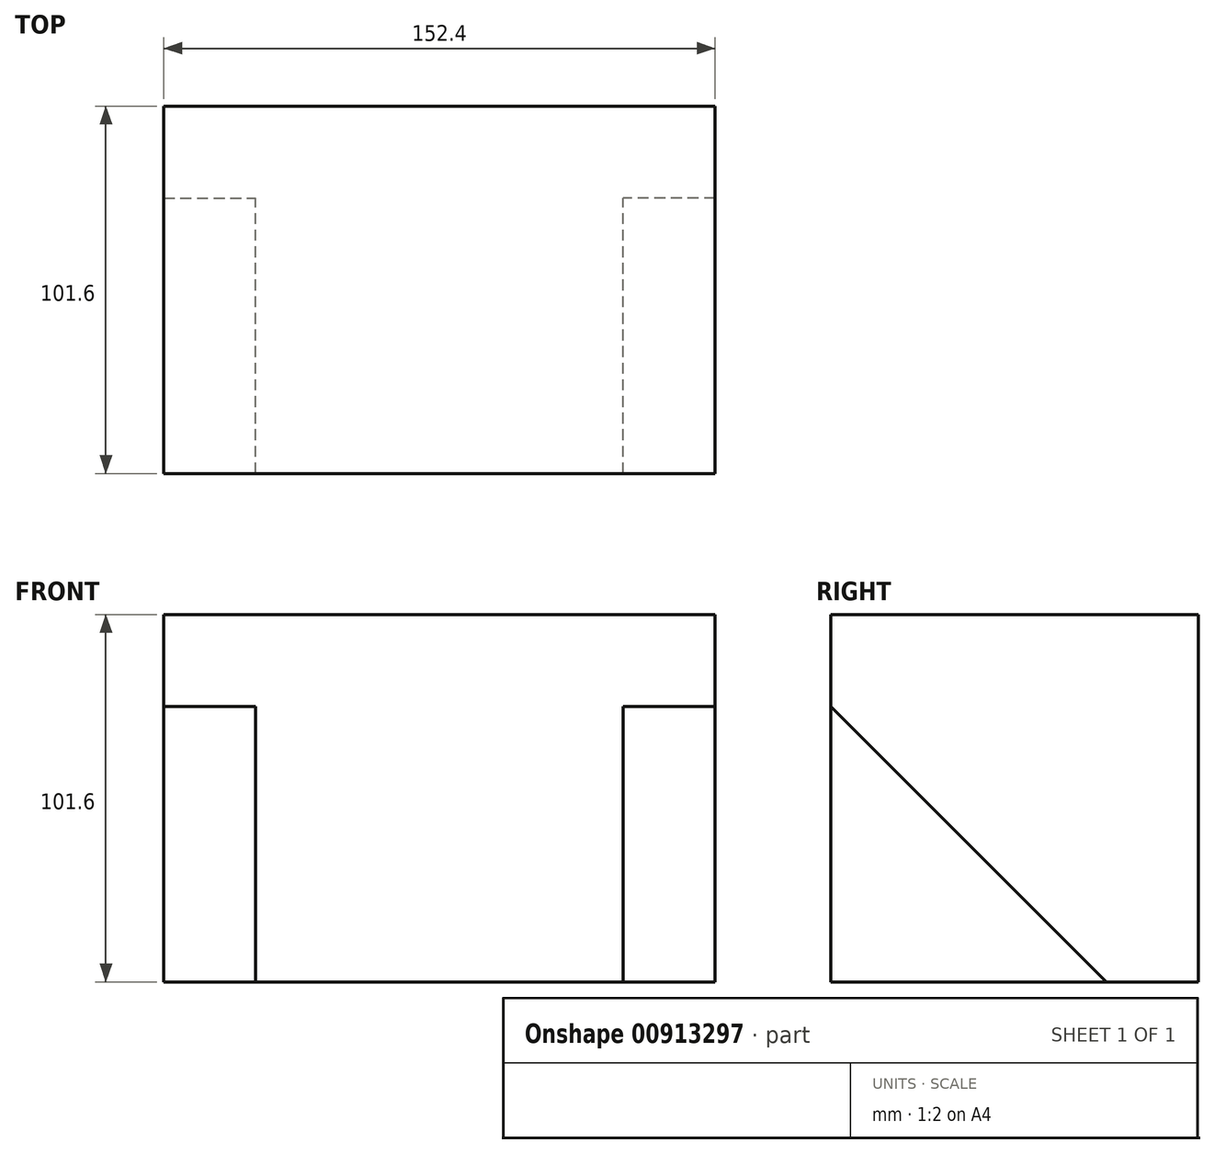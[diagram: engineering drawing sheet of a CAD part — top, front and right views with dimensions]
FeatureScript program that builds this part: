
annotation { "Feature Type Name" : "Feature", "Feature Type Description" : "" }
export const myFeature = defineFeature(function(context is Context, id is Id, definition is map)
    precondition{}
    {
        {
            var Q0;
            Q0=qCreatedBy(makeId("Top.planeOp"),FACE);
            var sketch = newSketch(context, id + "F0", { "sketchPlane" : qUnion([Q0])});
            skLineSegment(sketch, "E0.bottom", {"start": v(0, 0) * mm, "end": v(-101.6, 0) * mm});
            skLineSegment(sketch, "E0.top", {"start": v(0, 101.6) * mm, "end": v(-101.6, 101.6) * mm});
            skLineSegment(sketch, "E0.left", {"start": v(0, 0) * mm, "end": v(0, 101.6) * mm});
            skLineSegment(sketch, "E0.right", {"start": v(-101.6, 0) * mm, "end": v(-101.6, 101.6) * mm});
            skSolve(sketch);
        }
        {
            var Q0;
            Q0 = qSketchRegion(id + "F0", true);
            extrude(context, id + "F1", {"entities" : qUnion([Q0]), "depth" : 101.6 * mm, "offsetDistance" : 25.4 * mm});
        }
        {
            var Q0;
            Q0=makeQuery(id+"F1.opExtrude","CAP_FACE",FACE,{"disambiguationData":[OSD([sQuery(id+"F0.wireOp",EDGE,"E0.bottom"),sQuery(id+"F0.wireOp",EDGE,"E0.top"),sQuery(id+"F0.wireOp",EDGE,"E0.left"),sQuery(id+"F0.wireOp",EDGE,"E0.right")])],"isStart":false});
            var sketch = newSketch(context, id + "F2", { "sketchPlane" : qUnion([Q0])});
            skLineSegment(sketch, "E1.bottom", {"start": v(0, 0) * mm, "end": v(25.4, 0) * mm});
            skLineSegment(sketch, "E1.top", {"start": v(0, 101.6) * mm, "end": v(25.4, 101.6) * mm});
            skLineSegment(sketch, "E1.left", {"start": v(0, 0) * mm, "end": v(0, 101.6) * mm});
            skLineSegment(sketch, "E1.right", {"start": v(25.4, 0) * mm, "end": v(25.4, 101.6) * mm});
            skSolve(sketch);
        }
        {
            var Q0;
            Q0 = qSketchRegion(id + "F2", true);
            extrude(context, id + "F3", {"entities" : qUnion([Q0]), "oppositeDirection" : true, "depth" : 25.4 * mm, "offsetDistance" : 25.4 * mm});
        }
        {
            var Q0;
            Q0=makeQuery(id+"F1.opExtrude","SWEPT_FACE",FACE,{"disambiguationData":[OSD([sQuery(id+"F0.wireOp",EDGE,"E0.left")])]});
            var sketch = newSketch(context, id + "F4", { "sketchPlane" : qUnion([Q0])});
            skLineSegment(sketch, "E2.bottom", {"start": v(101.6, 0) * mm, "end": v(76.2, 0) * mm});
            skLineSegment(sketch, "E2.top", {"start": v(101.6, 76.2) * mm, "end": v(76.2, 76.2) * mm});
            skLineSegment(sketch, "E2.left", {"start": v(101.6, 0) * mm, "end": v(101.6, 76.2) * mm});
            skLineSegment(sketch, "E2.right", {"start": v(76.2, 0) * mm, "end": v(76.2, 76.2) * mm});
            skSolve(sketch);
        }
        {
            var Q0;
            Q0 = qSketchRegion(id + "F4", true);
            extrude(context, id + "F5", {"entities" : qUnion([Q0]), "depth" : 25.4 * mm, "offsetDistance" : 25.4 * mm});
        }
        {
            var Q0;
            Q0=makeQuery(id+"F1.opExtrude","SWEPT_FACE",FACE,{"disambiguationData":[OSD([sQuery(id+"F0.wireOp",EDGE,"E0.left")])]});
            var sketch = newSketch(context, id + "F6", { "sketchPlane" : qUnion([Q0])});
            skLineSegment(sketch, "E3.bottom", {"start": v(0, 0) * mm, "end": v(76.2, 0) * mm});
            skLineSegment(sketch, "E3.top", {"start": v(0, 76.2) * mm, "end": v(76.2, 76.2) * mm});
            skLineSegment(sketch, "E3.left", {"start": v(0, 0) * mm, "end": v(0, 76.2) * mm});
            skLineSegment(sketch, "E3.right", {"start": v(76.2, 0) * mm, "end": v(76.2, 76.2) * mm});
            skLineSegment(sketch, "E4", {"start": v(0, 76.2) * mm, "end": v(76.2, 0) * mm});
            skSolve(sketch);
        }
        {
            var Q0;
            Q0=makeQuery(id+"F6.imprint","IMPRINT",FACE,{"disambiguationData":[TD([[makeQuery(id+"F6.imprint","IMPRINT",EDGE,{"derivedFrom":sQuery(id+"F6.wireOp",EDGE,"E3.top")}),-1.0]])]});
            extrude(context, id + "F7", {"entities" : qUnion([Q0]), "operationType" : NewBodyOperationType.ADD, "depth" : 25.4 * mm, "offsetDistance" : 25.4 * mm});
        }
        {
            var Q0;
            Q0=makeQuery(id+"F1.opExtrude","SWEPT_FACE",FACE,{"disambiguationData":[OSD([sQuery(id+"F0.wireOp",EDGE,"E0.right")])]});
            var sketch = newSketch(context, id + "F8", { "sketchPlane" : qUnion([Q0])});
            skLineSegment(sketch, "E5.bottom", {"start": v(-101.6, 0) * mm, "end": v(-76.2, 0) * mm});
            skLineSegment(sketch, "E5.top", {"start": v(-101.6, 101.6) * mm, "end": v(-76.2, 101.6) * mm});
            skLineSegment(sketch, "E5.left", {"start": v(-101.6, 0) * mm, "end": v(-101.6, 101.6) * mm});
            skLineSegment(sketch, "E5.right", {"start": v(-76.2, 0) * mm, "end": v(-76.2, 101.6) * mm});
            skSolve(sketch);
        }
        {
            var Q0;
            Q0 = qSketchRegion(id + "F8", true);
            extrude(context, id + "F9", {"entities" : qUnion([Q0]), "operationType" : NewBodyOperationType.ADD, "depth" : 25.4 * mm, "offsetDistance" : 25.4 * mm});
        }
        {
            var Q0;
            Q0=makeQuery(id+"F1.opExtrude","SWEPT_FACE",FACE,{"disambiguationData":[OSD([sQuery(id+"F0.wireOp",EDGE,"E0.right")])]});
            var sketch = newSketch(context, id + "F10", { "sketchPlane" : qUnion([Q0])});
            skLineSegment(sketch, "E6.bottom", {"start": v(0, 101.6) * mm, "end": v(-76.2, 101.6) * mm});
            skLineSegment(sketch, "E6.top", {"start": v(0, 76.2) * mm, "end": v(-76.2, 76.2) * mm});
            skLineSegment(sketch, "E6.left", {"start": v(0, 101.6) * mm, "end": v(0, 76.2) * mm});
            skLineSegment(sketch, "E6.right", {"start": v(-76.2, 101.6) * mm, "end": v(-76.2, 76.2) * mm});
            skSolve(sketch);
        }
        {
            var Q0;
            Q0 = qSketchRegion(id + "F10", true);
            extrude(context, id + "F11", {"entities" : qUnion([Q0]), "operationType" : NewBodyOperationType.ADD, "depth" : 25.4 * mm, "offsetDistance" : 25.4 * mm});
        }
        {
            var Q0;
            Q0=makeQuery(id+"F1.opExtrude","SWEPT_FACE",FACE,{"disambiguationData":[OSD([sQuery(id+"F0.wireOp",EDGE,"E0.right")])]});
            var sketch = newSketch(context, id + "F12", { "sketchPlane" : qUnion([Q0])});
            skLineSegment(sketch, "E7.bottom", {"start": v(-76.2, 76.2) * mm, "end": v(0, 76.2) * mm});
            skLineSegment(sketch, "E7.top", {"start": v(-76.2, 0) * mm, "end": v(0, 0) * mm});
            skLineSegment(sketch, "E7.left", {"start": v(-76.2, 76.2) * mm, "end": v(-76.2, 0) * mm});
            skLineSegment(sketch, "E7.right", {"start": v(0, 76.2) * mm, "end": v(0, 0) * mm});
            skLineSegment(sketch, "E8", {"start": v(0, 76.2) * mm, "end": v(-76.2, 0) * mm});
            skSolve(sketch);
        }
        {
            var Q0;
            Q0=makeQuery(id+"F12.imprint","IMPRINT",FACE,{"disambiguationData":[TD([[makeQuery(id+"F12.imprint","IMPRINT",EDGE,{"derivedFrom":sQuery(id+"F12.wireOp",EDGE,"E7.bottom")}),1.0]])]});
            extrude(context, id + "F13", {"entities" : qUnion([Q0]), "operationType" : NewBodyOperationType.ADD, "depth" : 25.4 * mm, "offsetDistance" : 25.4 * mm});
        }
    });
